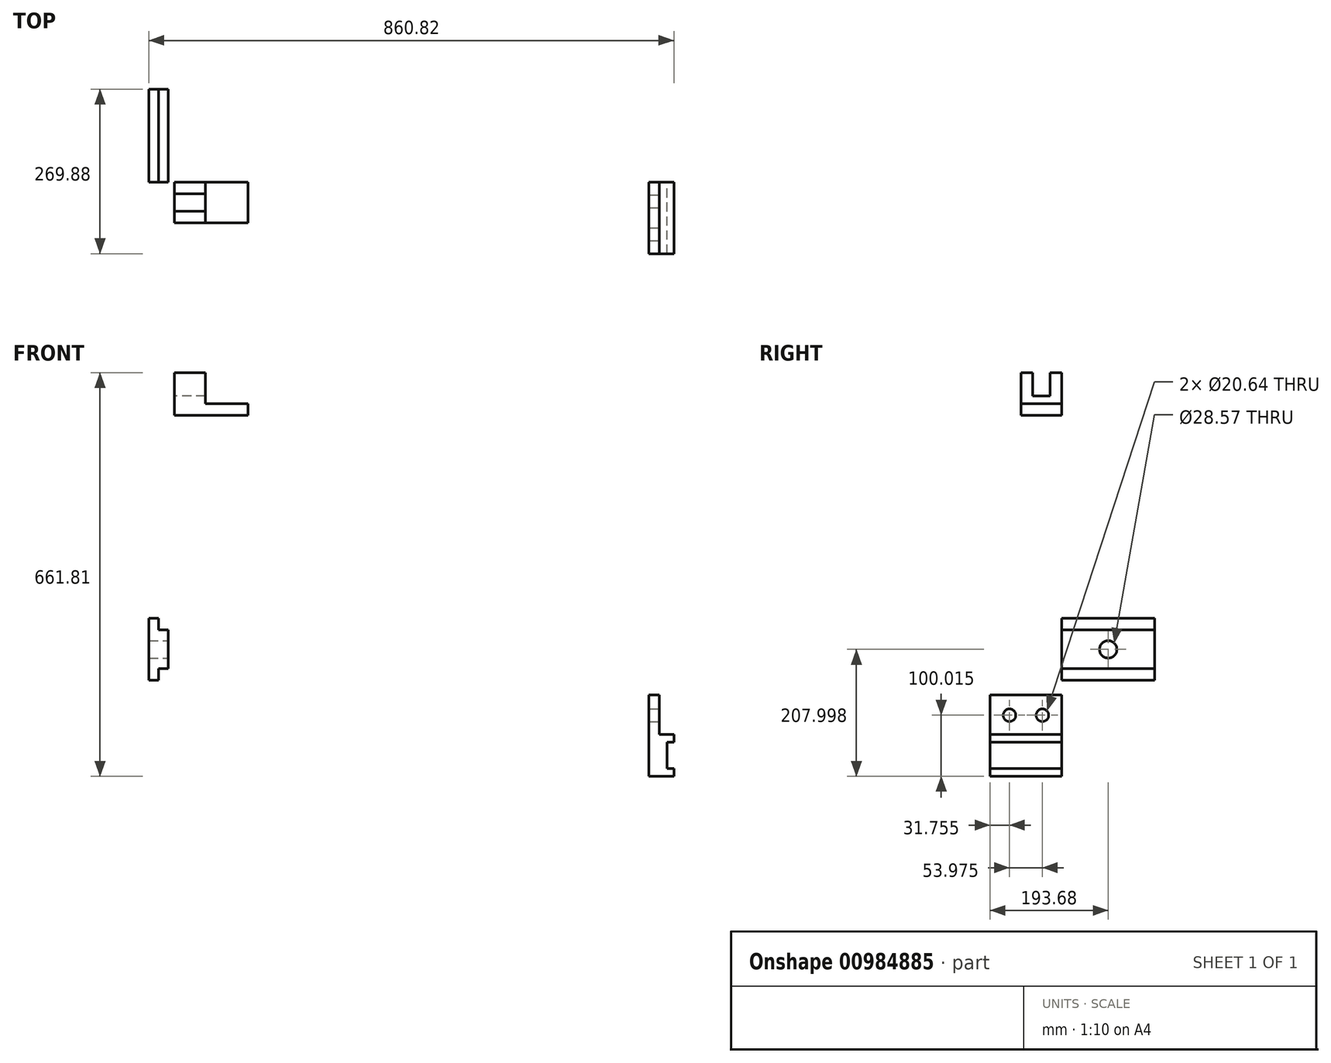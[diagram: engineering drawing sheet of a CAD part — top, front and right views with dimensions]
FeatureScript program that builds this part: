
annotation { "Feature Type Name" : "Feature", "Feature Type Description" : "" }
export const myFeature = defineFeature(function(context is Context, id is Id, definition is map)
    precondition{}
    {
        {
            var Q0;
            Q0=qCreatedBy(makeId("Front.planeOp"),FACE);
            var sketch = newSketch(context, id + "F0", { "sketchPlane" : qUnion([Q0])});
            skLineSegment(sketch, "E0.bottom", {"start": v(-15.88, 48.96) * mm, "end": v(15.87, 48.96) * mm});
            skLineSegment(sketch, "E0.top", {"start": v(-15.88, -52.64) * mm, "end": v(15.87, -52.64) * mm});
            skLineSegment(sketch, "E0.left", {"start": v(-15.88, 48.96) * mm, "end": v(-15.88, -52.64) * mm});
            skLineSegment(sketch, "E0.right", {"start": v(15.87, 48.96) * mm, "end": v(15.87, -52.64) * mm});
            skLineSegment(sketch, "E1.bottom", {"start": v(15.87, 48.96) * mm, "end": v(0, 48.96) * mm});
            skLineSegment(sketch, "E1.top", {"start": v(15.87, 29.9) * mm, "end": v(0, 29.9) * mm});
            skLineSegment(sketch, "E1.left", {"start": v(15.87, 48.96) * mm, "end": v(15.87, 29.9) * mm});
            skLineSegment(sketch, "E1.right", {"start": v(0, 48.96) * mm, "end": v(0, 29.9) * mm});
            skLineSegment(sketch, "E2.bottom", {"start": v(15.87, -52.64) * mm, "end": v(0, -52.64) * mm});
            skLineSegment(sketch, "E2.top", {"start": v(15.87, -33.6) * mm, "end": v(0, -33.6) * mm});
            skLineSegment(sketch, "E2.left", {"start": v(15.88, -52.64) * mm, "end": v(15.87, -33.6) * mm});
            skLineSegment(sketch, "E2.right", {"start": v(0, -52.64) * mm, "end": v(0, -33.6) * mm});
            skSolve(sketch);
        }
        {
            var Q0;
            {var subQ3=sQuery(id+"F0.wireOp",EDGE,"E0.left");Q0=makeQuery(id+"F0.imprint","IMPRINT",FACE,{"disambiguationData":[TD([[makeQuery(id+"F0.imprint","IMPRINT",EDGE,{"derivedFrom":subQ3}),1.0]])]});}
            extrude(context, id + "F1", {"entities" : qUnion([Q0]), "depth" : 152.4 * mm, "offsetDistance" : 25.4 * mm});
        }
        {
            var Q0;
            Q0=makeQuery(id+"F1.opExtrude","SWEPT_FACE",FACE,{"disambiguationData":[OSD([sQuery(id+"F0.wireOp",EDGE,"E0.right")])]});
            var sketch = newSketch(context, id + "F2", { "sketchPlane" : qUnion([Q0])});
            skCircle(sketch, "E3", {"center": v(-76.2, -1.84) * mm, "radius": 14.29 * mm});
            skSolve(sketch);
        }
        {
            var Q0;
            Q0=makeQuery(id+"F2.imprint","IMPRINT",FACE,{"disambiguationData":[TD([[makeQuery(id+"F2.imprint","IMPRINT",EDGE,{"derivedFrom":sQuery(id+"F2.wireOp",EDGE,"E3")}),1.0]])]});
            extrude(context, id + "F3", {"entities" : qUnion([Q0]), "operationType" : NewBodyOperationType.REMOVE, "oppositeDirection" : true, "depth" : 25.4 * mm, "offsetDistance" : 25.4 * mm});
        }
        {
            var Q0;
            Q0=makeQuery(id+"F3.boolean.opBoolean","COPY",FACE,{"derivedFrom":makeQuery(id+"F3.opExtrude","CAP_FACE",FACE,{"disambiguationData":[OSD([sQuery(id+"F2.wireOp",EDGE,"E3")])],"isStart":false})});
            extrude(context, id + "F4", {"entities" : qUnion([Q0]), "operationType" : NewBodyOperationType.REMOVE, "endBound" : BoundingType.THROUGH_ALL, "oppositeDirection" : true, "depth" : 25.4 * mm, "offsetDistance" : 25.4 * mm});
        }
        {
            var Q0;
            Q0=makeQuery(id+"F1.opExtrude","CAP_FACE",FACE,{"disambiguationData":[OSD([sQuery(id+"F0.wireOp",EDGE,"E0.bottom"),sQuery(id+"F0.wireOp",EDGE,"E0.top"),sQuery(id+"F0.wireOp",EDGE,"E0.left"),sQuery(id+"F0.wireOp",EDGE,"E0.right"),sQuery(id+"F0.wireOp",EDGE,"E1.top"),sQuery(id+"F0.wireOp",EDGE,"E1.right"),sQuery(id+"F0.wireOp",EDGE,"E2.top"),sQuery(id+"F0.wireOp",EDGE,"E2.right")])],"isStart":false});
            var sketch = newSketch(context, id + "F5", { "sketchPlane" : qUnion([Q0])});
            skLineSegment(sketch, "E4.bottom", {"start": v(803.66, -76.49) * mm, "end": v(844.94, -76.49) * mm});
            skLineSegment(sketch, "E4.top", {"start": v(803.66, -209.84) * mm, "end": v(844.94, -209.84) * mm});
            skLineSegment(sketch, "E4.left", {"start": v(803.66, -76.49) * mm, "end": v(803.66, -209.84) * mm});
            skLineSegment(sketch, "E4.right", {"start": v(844.94, -76.49) * mm, "end": v(844.94, -209.84) * mm});
            skLineSegment(sketch, "E5.bottom", {"start": v(844.94, -76.49) * mm, "end": v(827.48, -76.49) * mm});
            skLineSegment(sketch, "E5.left", {"start": v(844.94, -76.49) * mm, "end": v(844.94, -109.82) * mm});
            skLineSegment(sketch, "E6.bottom", {"start": v(844.94, -209.84) * mm, "end": v(827.48, -209.84) * mm});
            skLineSegment(sketch, "E6.left", {"start": v(844.94, -209.84) * mm, "end": v(844.94, -154.27) * mm});
            skLineSegment(sketch, "E7.left", {"start": v(844.94, -196.4) * mm, "end": v(844.94, -156.62) * mm});
            skLineSegment(sketch, "E8.bottom", {"start": v(844.94, -154.27) * mm, "end": v(833.83, -154.27) * mm});
            skLineSegment(sketch, "E8.top", {"start": v(844.94, -197.14) * mm, "end": v(833.83, -197.14) * mm});
            skLineSegment(sketch, "E8.left", {"start": v(844.94, -154.27) * mm, "end": v(844.94, -197.14) * mm});
            skLineSegment(sketch, "E8.right", {"start": v(833.83, -154.27) * mm, "end": v(833.83, -197.14) * mm});
            skLineSegment(sketch, "E9.top", {"start": v(844.94, -141.57) * mm, "end": v(821.13, -141.57) * mm});
            skLineSegment(sketch, "E9.left", {"start": v(844.94, -78.77) * mm, "end": v(844.94, -141.57) * mm});
            skLineSegment(sketch, "E9.right", {"start": v(821.13, -76.49) * mm, "end": v(821.13, -141.57) * mm});
            skSolve(sketch);
        }
        {
            var Q0;
            Q0=makeQuery(id+"F5.imprint","IMPRINT",FACE,{"disambiguationData":[TD([[makeQuery(id+"F5.imprint","IMPRINT",EDGE,{"derivedFrom":sQuery(id+"F5.wireOp",EDGE,"E4.top")}),1.0]])]});
            extrude(context, id + "F6", {"entities" : qUnion([Q0]), "depth" : 117.47 * mm, "offsetDistance" : 25.4 * mm});
        }
        {
            var Q0;
            Q0=makeQuery(id+"F6.opExtrude","CAP_FACE",FACE,{"disambiguationData":[OSD([sQuery(id+"F5.wireOp",EDGE,"E4.bottom"),sQuery(id+"F5.wireOp",EDGE,"E4.top"),sQuery(id+"F5.wireOp",EDGE,"E4.left"),sQuery(id+"F5.wireOp",EDGE,"E4.right"),sQuery(id+"F5.wireOp",EDGE,"E5.bottom"),sQuery(id+"F5.wireOp",EDGE,"E5.left"),sQuery(id+"F5.wireOp",EDGE,"E6.bottom"),sQuery(id+"F5.wireOp",EDGE,"E6.left"),sQuery(id+"F5.wireOp",EDGE,"E7.left"),sQuery(id+"F5.wireOp",EDGE,"E8.bottom"),sQuery(id+"F5.wireOp",EDGE,"E8.top"),sQuery(id+"F5.wireOp",EDGE,"E8.right"),sQuery(id+"F5.wireOp",EDGE,"E9.bottom"),sQuery(id+"F5.wireOp",EDGE,"E9.top"),sQuery(id+"F5.wireOp",EDGE,"E9.right")])],"isStart":false});
            var sketch = newSketch(context, id + "F7", { "sketchPlane" : qUnion([Q0])});
            skSolve(sketch);
        }
        {
            var Q0;
            Q0=makeQuery(id+"F6.opExtrude","SWEPT_FACE",FACE,{"disambiguationData":[OSD([sQuery(id+"F5.wireOp",EDGE,"E9.right")])]});
            var sketch = newSketch(context, id + "F8", { "sketchPlane" : qUnion([Q0])});
            skCircle(sketch, "E10", {"center": v(-184.15, -109.82) * mm, "radius": 10.32 * mm});
            skCircle(sketch, "E11", {"center": v(-238.12, -109.82) * mm, "radius": 10.32 * mm});
            skSolve(sketch);
        }
        {
            var Q0;
            Q0 = qSketchRegion(id + "F8", true);
            extrude(context, id + "F9", {"entities" : qUnion([Q0]), "operationType" : NewBodyOperationType.REMOVE, "endBound" : BoundingType.THROUGH_ALL, "oppositeDirection" : true, "depth" : 25.4 * mm, "offsetDistance" : 25.4 * mm});
        }
        {
            var Q0;
            Q0=makeQuery(id+"F6.opExtrude","SWEPT_FACE",FACE,{"disambiguationData":[OSD([sQuery(id+"F5.wireOp",EDGE,"E9.right")])]});
            var sketch = newSketch(context, id + "F10", { "sketchPlane" : qUnion([Q0])});
            skText(sketch, "E12", { "text": "Summer ", "fontName": "OpenSans-Regular.ttf"});
            const initialGuessF10  = {"E12": [-0.705, 0.0522, 1, 0, 0.09245]};
            skSetInitialGuess(sketch, initialGuessF10);
            skSolve(sketch);
        }
        {
            var Q0;
            Q0 = qConstructionFilter(qBodyType(qCreatedBy(id + "F10" ,EDGE), BodyType.WIRE), ConstructionObject.NO);
            extrude(context, id + "F11", {"bodyType" : ToolBodyType.SURFACE, "surfaceEntities" : qUnion([Q0]), "depth" : 50.8 * mm, "offsetDistance" : 25.4 * mm});
        }
        {
            var Q0;
            Q0=makeQuery(id+"F1.opExtrude","CAP_FACE",FACE,{"disambiguationData":[OSD([sQuery(id+"F0.wireOp",EDGE,"E0.bottom"),sQuery(id+"F0.wireOp",EDGE,"E0.top"),sQuery(id+"F0.wireOp",EDGE,"E0.left"),sQuery(id+"F0.wireOp",EDGE,"E0.right"),sQuery(id+"F0.wireOp",EDGE,"E1.top"),sQuery(id+"F0.wireOp",EDGE,"E1.right"),sQuery(id+"F0.wireOp",EDGE,"E2.top"),sQuery(id+"F0.wireOp",EDGE,"E2.right")])],"isStart":false});
            var sketch = newSketch(context, id + "F12", { "sketchPlane" : qUnion([Q0])});
            skLineSegment(sketch, "E13.bottom", {"start": v(25.82, 426.57) * mm, "end": v(146.47, 426.57) * mm});
            skLineSegment(sketch, "E13.top", {"start": v(25.82, 382.12) * mm, "end": v(146.47, 382.12) * mm});
            skLineSegment(sketch, "E13.left", {"start": v(25.82, 426.57) * mm, "end": v(25.82, 382.12) * mm});
            skLineSegment(sketch, "E13.right", {"start": v(146.47, 426.57) * mm, "end": v(146.47, 382.12) * mm});
            skLineSegment(sketch, "E14.bottom", {"start": v(51.22, 426.57) * mm, "end": v(146.47, 426.57) * mm});
            skLineSegment(sketch, "E14.top", {"start": v(51.22, 401.17) * mm, "end": v(146.47, 401.17) * mm});
            skLineSegment(sketch, "E14.left", {"start": v(51.22, 426.57) * mm, "end": v(51.22, 401.17) * mm});
            skLineSegment(sketch, "E14.right", {"start": v(146.47, 426.57) * mm, "end": v(146.47, 401.17) * mm});
            skSolve(sketch);
        }
        {
            var Q0;
            {var subQ1=sQuery(id+"F12.wireOp",EDGE,"E13.top");Q0=makeQuery(id+"F12.imprint","IMPRINT",FACE,{"disambiguationData":[TD([[makeQuery(id+"F12.imprint","IMPRINT",EDGE,{"derivedFrom":subQ1}),1.0]])]});}
            extrude(context, id + "F13", {"entities" : qUnion([Q0]), "depth" : 66.67 * mm, "offsetDistance" : 25.4 * mm});
        }
        {
            var Q0;
            Q0=makeQuery(id+"F13.opExtrude","SWEPT_FACE",FACE,{"disambiguationData":[OSD([sQuery(id+"F12.wireOp",EDGE,"E14.left")])]});
            var sketch = newSketch(context, id + "F14", { "sketchPlane" : qUnion([Q0])});
            skLineSegment(sketch, "E15.bottom", {"start": v(-200.03, 426.57) * mm, "end": v(-171.45, 426.57) * mm});
            skLineSegment(sketch, "E15.top", {"start": v(-200.03, 413.87) * mm, "end": v(-171.45, 413.87) * mm});
            skLineSegment(sketch, "E15.left", {"start": v(-200.03, 426.57) * mm, "end": v(-200.03, 413.87) * mm});
            skLineSegment(sketch, "E15.right", {"start": v(-171.45, 426.57) * mm, "end": v(-171.45, 413.87) * mm});
            skSolve(sketch);
        }
        {
            var Q0;
            Q0=makeQuery(id+"F13.opExtrude","SWEPT_FACE",FACE,{"disambiguationData":[OSD([sQuery(id+"F12.wireOp",EDGE,"E13.bottom")])]});
            var sketch = newSketch(context, id + "F15", { "sketchPlane" : qUnion([Q0])});
            skLineSegment(sketch, "E16.bottom", {"start": v(25.82, -200.03) * mm, "end": v(51.22, -200.03) * mm});
            skLineSegment(sketch, "E16.top", {"start": v(25.82, -171.45) * mm, "end": v(51.22, -171.45) * mm});
            skLineSegment(sketch, "E16.left", {"start": v(25.82, -200.03) * mm, "end": v(25.82, -171.45) * mm});
            skLineSegment(sketch, "E16.right", {"start": v(51.22, -200.03) * mm, "end": v(51.22, -171.45) * mm});
            skSolve(sketch);
        }
        {
            var Q0;
            {var subQ0=sQuery(id+"F15.wireOp",EDGE,"E16.bottom");Q0=makeQuery(id+"F15.imprint","IMPRINT",FACE,{"disambiguationData":[TD([[makeQuery(id+"F15.imprint","IMPRINT",EDGE,{"derivedFrom":subQ0}),-1.0]])]});}
            var Q1;
            {var subQ0=sQuery(id+"F15.wireOp",EDGE,"E16.top");Q1=makeQuery(id+"F15.imprint","IMPRINT",FACE,{"disambiguationData":[TD([[makeQuery(id+"F15.imprint","IMPRINT",EDGE,{"derivedFrom":subQ0}),1.0]])]});}
            extrude(context, id + "F16", {"entities" : qUnion([Q0, Q1]), "operationType" : NewBodyOperationType.ADD, "depth" : 25.4 * mm, "offsetDistance" : 25.4 * mm});
        }
        {
            var Q0;
            Q0=makeQuery(id+"F14.imprint","IMPRINT",FACE,{"disambiguationData":[TD([[makeQuery(id+"F14.imprint","IMPRINT",EDGE,{"derivedFrom":sQuery(id+"F14.wireOp",EDGE,"E15.top")}),-1.0]])]});
            extrude(context, id + "F17", {"entities" : qUnion([Q0]), "operationType" : NewBodyOperationType.ADD, "depth" : 25.4 * mm, "offsetDistance" : 25.4 * mm});
        }
        {
            var Q0;
            {var subQ0=sQuery(id+"F12.wireOp",EDGE,"E14.left");var subQ1=sQuery(id+"F12.wireOp",EDGE,"E13.bottom");var subQ2=makeQuery(id+"F13.opExtrude","SWEPT_EDGE",EDGE,{"disambiguationData":[OSD([subQ1,subQ0])]});var subQ8=makeQuery(id+"F16.opExtrude","SWEPT_FACE",FACE,{"disambiguationData":[OSD([subQ1,subQ0]),TDD([makeQuery(id+"F15.imprint","IMPRINT",EDGE,{"disambiguationData":[TD([[makeQuery(id+"F15.imprint","INTERSECT",VERTEX,{"derivedFrom":[subQ2,makeQuery(id+"F13.opExtrude","CAP_EDGE",EDGE,{"disambiguationData":[OSD([subQ1])],"isStart":false})]}),-1.0]])],"derivedFrom":subQ2})])]});var subQ9=makeQuery(id+"F16.opExtrude","SWEPT_FACE",FACE,{"disambiguationData":[OSD([subQ1,subQ0]),TDD([makeQuery(id+"F15.imprint","IMPRINT",EDGE,{"disambiguationData":[TD([[makeQuery(id+"F15.imprint","INTERSECT",VERTEX,{"derivedFrom":[subQ2,makeQuery(id+"F13.opExtrude","CAP_EDGE",EDGE,{"disambiguationData":[OSD([subQ1])],"isStart":true})]}),1.0]])],"derivedFrom":subQ2})])]});var subQ10=makeQuery(id+"F13.opExtrude","SWEPT_FACE",FACE,{"disambiguationData":[OSD([subQ0])]});Q0=makeQuery(id+"F17.boolean.opBoolean","SPLIT",FACE,{"disambiguationData":[TD([makeQuery(id+"F17.opExtrude","SWEPT_FACE",FACE,{"disambiguationData":[OSD([sQuery(id+"F14.wireOp",EDGE,"E15.top")])]})])],"derivedFrom":makeQuery(id+"F16.boolean.opBoolean","MERGE",FACE,{"derivedFrom":[subQ10,subQ9,subQ8]})});}
            extrude(context, id + "F18", {"entities" : qUnion([Q0]), "operationType" : NewBodyOperationType.REMOVE, "endBound" : BoundingType.THROUGH_ALL, "oppositeDirection" : true, "depth" : 25.4 * mm, "offsetDistance" : 25.4 * mm});
        }
        {
            var Q0;
            {var subQ0=sQuery(id+"F12.wireOp",EDGE,"E14.left");var subQ1=sQuery(id+"F12.wireOp",EDGE,"E13.bottom");Q0=makeQuery(id+"F17.boolean.opBoolean","MERGE",FACE,{"derivedFrom":[makeQuery(id+"F16.boolean.opBoolean","MERGE",FACE,{"derivedFrom":[makeQuery(id+"F13.opExtrude","CAP_FACE",FACE,{"disambiguationData":[OSD([subQ1,sQuery(id+"F12.wireOp",EDGE,"E13.top"),sQuery(id+"F12.wireOp",EDGE,"E13.left"),sQuery(id+"F12.wireOp",EDGE,"E13.right"),sQuery(id+"F12.wireOp",EDGE,"E14.top"),subQ0])],"isStart":false}),makeQuery(id+"F16.opExtrude","SWEPT_FACE",FACE,{"disambiguationData":[OSD([subQ1]),TDD([makeQuery(id+"F15.imprint","IMPRINT",EDGE,{"derivedFrom":makeQuery(id+"F13.opExtrude","CAP_EDGE",EDGE,{"disambiguationData":[OSD([subQ1])],"isStart":false})})])]})]}),makeQuery(id+"F17.opExtrude","SWEPT_FACE",FACE,{"disambiguationData":[OSD([subQ0]),TDD([makeQuery(id+"F14.imprint","IMPRINT",EDGE,{"derivedFrom":makeQuery(id+"F13.opExtrude","CAP_EDGE",EDGE,{"disambiguationData":[OSD([subQ0])],"isStart":false})})])]})]});}
            var sketch = newSketch(context, id + "F19", { "sketchPlane" : qUnion([Q0])});
            skLineSegment(sketch, "E17.bottom", {"start": v(51.22, 451.97) * mm, "end": v(76.62, 451.97) * mm});
            skLineSegment(sketch, "E17.top", {"start": v(51.22, 426.57) * mm, "end": v(76.62, 426.57) * mm});
            skLineSegment(sketch, "E17.left", {"start": v(51.22, 451.97) * mm, "end": v(51.22, 426.57) * mm});
            skLineSegment(sketch, "E17.right", {"start": v(76.62, 451.97) * mm, "end": v(76.62, 426.57) * mm});
            skSolve(sketch);
        }
        {
            var Q0;
            Q0=makeQuery(id+"F19.imprint","IMPRINT",FACE,{"disambiguationData":[TD([[makeQuery(id+"F19.imprint","IMPRINT",EDGE,{"derivedFrom":sQuery(id+"F19.wireOp",EDGE,"E17.bottom")}),-1.0]])]});
            extrude(context, id + "F20", {"entities" : qUnion([Q0]), "operationType" : NewBodyOperationType.ADD, "oppositeDirection" : true, "depth" : 19.05 * mm, "offsetDistance" : 25.4 * mm});
        }
        {
            var Q0;
            {var subQ0=sQuery(id+"F12.wireOp",EDGE,"E13.bottom");var subQ1=sQuery(id+"F12.wireOp",EDGE,"E14.left");var subQ2=makeQuery(id+"F13.opExtrude","SWEPT_EDGE",EDGE,{"disambiguationData":[OSD([subQ0,subQ1])]});var subQ4=makeQuery(id+"F16.opExtrude","SWEPT_FACE",FACE,{"disambiguationData":[OSD([subQ0,subQ1]),TDD([makeQuery(id+"F15.imprint","IMPRINT",EDGE,{"disambiguationData":[TD([[makeQuery(id+"F15.imprint","INTERSECT",VERTEX,{"derivedFrom":[subQ2,makeQuery(id+"F13.opExtrude","CAP_EDGE",EDGE,{"disambiguationData":[OSD([subQ0])],"isStart":false})]}),-1.0]])],"derivedFrom":subQ2})])]});var subQ5=makeQuery(id+"F13.opExtrude","CAP_EDGE",EDGE,{"disambiguationData":[OSD([subQ0])],"isStart":true});var subQ10=makeQuery(id+"F16.opExtrude","SWEPT_FACE",FACE,{"disambiguationData":[OSD([subQ0,subQ1]),TDD([makeQuery(id+"F15.imprint","IMPRINT",EDGE,{"disambiguationData":[TD([[makeQuery(id+"F15.imprint","INTERSECT",VERTEX,{"derivedFrom":[subQ2,subQ5]}),1.0]])],"derivedFrom":subQ2})])]});var subQ11=makeQuery(id+"F13.opExtrude","SWEPT_FACE",FACE,{"disambiguationData":[OSD([subQ1])]});Q0=makeQuery(id+"F17.boolean.opBoolean","SPLIT",FACE,{"disambiguationData":[TD([makeQuery(id+"F16.opExtrude","SWEPT_FACE",FACE,{"disambiguationData":[OSD([subQ0]),TDD([makeQuery(id+"F15.imprint","IMPRINT",EDGE,{"derivedFrom":subQ5})])]})])],"derivedFrom":makeQuery(id+"F16.boolean.opBoolean","MERGE",FACE,{"derivedFrom":[subQ11,subQ10,subQ4]})});}
            extrude(context, id + "F21", {"entities" : qUnion([Q0]), "operationType" : NewBodyOperationType.ADD, "depth" : 25.4 * mm, "offsetDistance" : 25.4 * mm});
        }
    });
